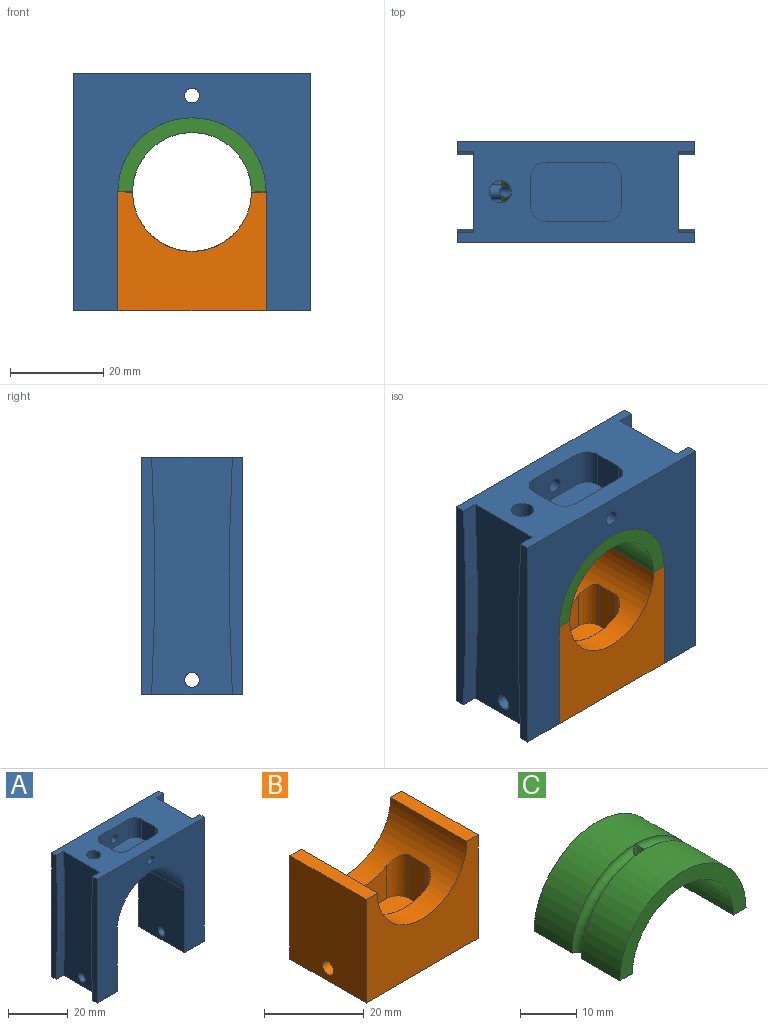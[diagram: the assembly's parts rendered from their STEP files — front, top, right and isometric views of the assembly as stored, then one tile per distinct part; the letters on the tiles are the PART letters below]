
ASSEMBLY  parts=3 mates=5
PART A: 42 faces, bbox 51x21.8x51 mm
  f0: cylinder r=15.88mm len=31.75mm, axis (0,1,0), area 1071.8mm2, adj f6,f7,f10,f11,f39
  f1: plane 50.8x21.59mm, normal (0,0,1), area 720.2mm2, adj f2,f3,f4,f9,f10,f11,f12,f17
  f2: plane 50.8x2.79mm, normal (1,0,0), area 130.3mm2, adj f1,f8,f11,f22,f23,f24
  f3: plane 50.8x2.79mm, normal (-1,0,0), area 130.3mm2, adj f1,f5,f11,f12,f13,f14
  f4: plane 50.8x2.79mm, normal (-1,0,0), area 130.3mm2, adj f1,f5,f10,f15,f16,f17
  f5: plane 21.59x9.53mm, normal (0,0,-1), area 145.3mm2, adj f3,f4,f6,f10,f11,f14,f15,f18
  f6: plane 25.4x21.59mm, normal (1,0,0), area 540.5mm2, adj f0,f5,f10,f11,f41
  f7: plane 25.4x21.59mm, normal (-1,0,0), area 540.5mm2, adj f0,f8,f10,f11,f40
  f8: plane 21.59x9.53mm, normal (0,0,-1), area 145.3mm2, adj f2,f7,f9,f10,f11,f21,f22,f25
  f9: plane 50.8x2.79mm, normal (1,0,0), area 130.3mm2, adj f1,f8,f10,f19,f20,f21
  f10: plane 50.8x50.8mm, normal (0,-1,0), area 1370.4mm2, adj f0,f1,f4,f5,f6,f7,f8,f9
  f11: plane 50.8x50.8mm, normal (0,1,0), area 1370.4mm2, adj f0,f1,f2,f3,f5,f6,f7,f8
  f12: plane 18.26x3.49mm, normal (0,-1,0.03), area 63.8mm2, adj f1,f3,f13,f18
  f13: plane 14.29x3.49mm, normal (0,-1,0), area 49.9mm2, adj f3,f12,f14,f18
  f14: plane 18.26x3.49mm, normal (0,-1,-0.03), area 63.8mm2, adj f3,f5,f13,f18
  f15: plane 18.26x3.49mm, normal (0,1,-0.03), area 63.8mm2, adj f4,f5,f16,f18
  f16: plane 14.29x3.49mm, normal (0,1,0), area 49.9mm2, adj f4,f15,f17,f18
  f17: plane 18.26x3.49mm, normal (0,1,0.03), area 63.8mm2, adj f1,f4,f16,f18
  f18: plane 50.8x17.28mm, normal (-1,0,0), area 828.3mm2, adj f1,f5,f12,f13,f14,f15,f16,f17
  f19: plane 18.26x3.49mm, normal (0,1,0.03), area 63.8mm2, adj f1,f9,f20,f25
  f20: plane 14.29x3.49mm, normal (0,1,0), area 49.9mm2, adj f9,f19,f21,f25
  f21: plane 18.26x3.49mm, normal (0,1,-0.03), area 63.8mm2, adj f8,f9,f20,f25
  f22: plane 18.26x3.49mm, normal (0,-1,-0.03), area 63.8mm2, adj f2,f8,f23,f25
  f23: plane 14.29x3.49mm, normal (0,-1,0), area 49.9mm2, adj f2,f22,f24,f25
  f24: plane 18.26x3.49mm, normal (0,-1,0.03), area 63.8mm2, adj f1,f2,f23,f25
  f25: plane 50.8x17.28mm, normal (1,0,0), area 828.3mm2, adj f1,f8,f19,f20,f21,f22,f23,f24
  f26: plane 7.94x6.35mm, normal (1,0,0), area 50.4mm2, adj f1,f27,f33,f34
  f27: cylinder r=3.17mm len=7.94mm, axis (0,0,1), area 39.6mm2, adj f1,f26,f28,f34
  f28: plane 13.08x7.94mm, normal (0,1,0), area 95.9mm2, adj f1,f27,f29,f34,f36
  f29: cylinder r=3.17mm len=7.94mm, axis (0,0,1), area 39.6mm2, adj f1,f28,f30,f34
  f30: plane 7.94x6.35mm, normal (-1,0,0), area 50.4mm2, adj f1,f29,f31,f34
  f31: cylinder r=3.17mm len=7.94mm, axis (0,0,1), area 39.6mm2, adj f1,f30,f32,f34
  f32: plane 13.08x7.94mm, normal (0,-1,0), area 95.9mm2, adj f1,f31,f33,f34,f35
  f33: cylinder r=3.17mm len=7.94mm, axis (0,0,1), area 39.6mm2, adj f1,f26,f32,f34
  f34: plane 19.43x12.7mm, normal (0,0,1), area 238.1mm2, adj f26,f27,f28,f29,f30,f31,f32,f33
  f35: cylinder r=1.59mm len=4.45mm, axis (0,-1,0), area 44.3mm2, adj f11,f32
  f36: cylinder r=1.59mm len=4.45mm, axis (0,-1,0), area 44.3mm2, adj f10,f28
  f37: cylinder r=2.38mm len=5.56mm, axis (0,0,1), area 83.1mm2, adj f1,f38
  f38: plane 4.96x4.96mm, normal (0,0,1), area 13mm2, adj f37,f39
  f39: cylinder r=1.19mm len=10.84mm, axis (0.37,0,-0.93), area 72.2mm2, adj f0,f38
  f40: cylinder r=1.59mm len=6.03mm, axis (1,0,0), area 60.2mm2, adj f7,f25
  f41: cylinder r=1.59mm len=6.03mm, axis (1,0,0), area 60.2mm2, adj f6,f18
PART B: 18 faces, bbox 31.8x21.6x25.4 mm
  f0: plane 25.4x21.59mm, normal (-1,0,0), area 540.5mm2, adj f1,f5,f6,f7,f17
  f1: plane 31.75x21.59mm, normal (0,0,-1), area 685.5mm2, adj f0,f2,f6,f7
  f2: plane 25.4x21.59mm, normal (1,0,0), area 540.5mm2, adj f1,f3,f6,f7,f17
  f3: plane 21.59x3.18mm, normal (0,0,1), area 68.5mm2, adj f2,f4,f6,f7
  f4: cylinder r=12.7mm len=25.4mm, axis (0,1,0), area 634.1mm2, adj f3,f5,f6,f7,f8,f9,f10,f11
  f5: plane 21.59x3.18mm, normal (0,0,1), area 68.5mm2, adj f0,f4,f6,f7
  f6: plane 31.75x25.4mm, normal (0,-1,0), area 553.1mm2, adj f0,f1,f2,f3,f4,f5
  f7: plane 31.75x25.4mm, normal (0,1,0), area 553.1mm2, adj f0,f1,f2,f3,f4,f5
  f8: plane 10.65x4.76mm, normal (1,0,0), area 50.7mm2, adj f4,f9,f15,f16
  f9: cylinder r=3.17mm len=10.65mm, axis (0,0,1), area 47.8mm2, adj f4,f8,f10,f16
  f10: plane 12.7x8.05mm, normal (0,1,0), area 87.6mm2, adj f4,f9,f11,f16
  f11: cylinder r=3.17mm len=10.65mm, axis (0,0,1), area 47.8mm2, adj f4,f10,f12,f16
  f12: plane 10.65x4.76mm, normal (-1,0,0), area 50.7mm2, adj f4,f11,f13,f16
  f13: cylinder r=3.17mm len=10.65mm, axis (0,0,1), area 47.8mm2, adj f4,f12,f14,f16
  f14: plane 12.7x8.05mm, normal (0,-1,0), area 87.6mm2, adj f4,f13,f15,f16
  f15: cylinder r=3.17mm len=10.65mm, axis (0,0,1), area 47.8mm2, adj f4,f8,f14,f16
  f16: plane 19.05x11.11mm, normal (0,0,1), area 203mm2, adj f8,f9,f10,f11,f12,f13,f14,f15
  f17: cylinder r=1.59mm len=31.75mm, axis (1,0,0), area 316.7mm2, adj f0,f2
PART C: 10 faces, bbox 36.2x21.6x18.1 mm
  f0: cylinder r=12.7mm len=25.4mm, axis (0,1,0), area 857mm2, adj f4,f5,f7,f8,f9
  f1: torus R=15.88mm, axis (0,-1,0), area 86mm2, adj f3,f6,f7,f9
  f2: torus R=15.88mm, axis (0,-1,0), area 86mm2, adj f3,f5,f6,f9
  f3: cylinder r=15.88mm len=31.75mm, axis (0,1,0), area 479mm2, adj f1,f2,f4,f5,f7
  f4: plane 31.75x15.88mm, normal (0,-1,0), area 142.5mm2, adj f0,f3,f5,f7
  f5: plane 21.59x3.18mm, normal (0,0,-1), area 66.3mm2, adj f0,f2,f3,f4,f6,f8
  f6: cylinder r=15.88mm len=31.75mm, axis (0,1,0), area 479mm2, adj f1,f2,f5,f7,f8
  f7: plane 21.59x3.18mm, normal (0,0,-1), area 66.3mm2, adj f0,f1,f3,f4,f6,f8
  f8: plane 31.75x15.88mm, normal (0,1,0), area 142.5mm2, adj f0,f5,f6,f7
  f9: cylinder r=1.19mm len=3.23mm, axis (0,0,-1), area 18.1mm2, adj f0,f1,f2
PLACE A t=(20.53,5.98,-31.78)mm
PLACE B t=(20.53,5.98,-31.78)mm
PLACE C t=(20.53,5.98,-31.78)mm
MATE planar A.f10 <-> C.f4  axis (0,-1,0) through (20.53,-4.82,-26.37)mm
MATE cylindrical A.f0 <-> C.f3  axis (0,1,0) through (20.53,5.98,-31.78)mm
MATE planar B.f0 <-> A.f6  axis (-1,0,0) through (4.66,5.98,-44.34)mm
MATE planar B.f6 <-> A.f35  axis (0,-1,0) through (20.53,-4.82,-47.83)mm
MATE planar C.f5 <-> B.f3  axis (0,0,-1) through (34.82,16.77,-31.78)mm
